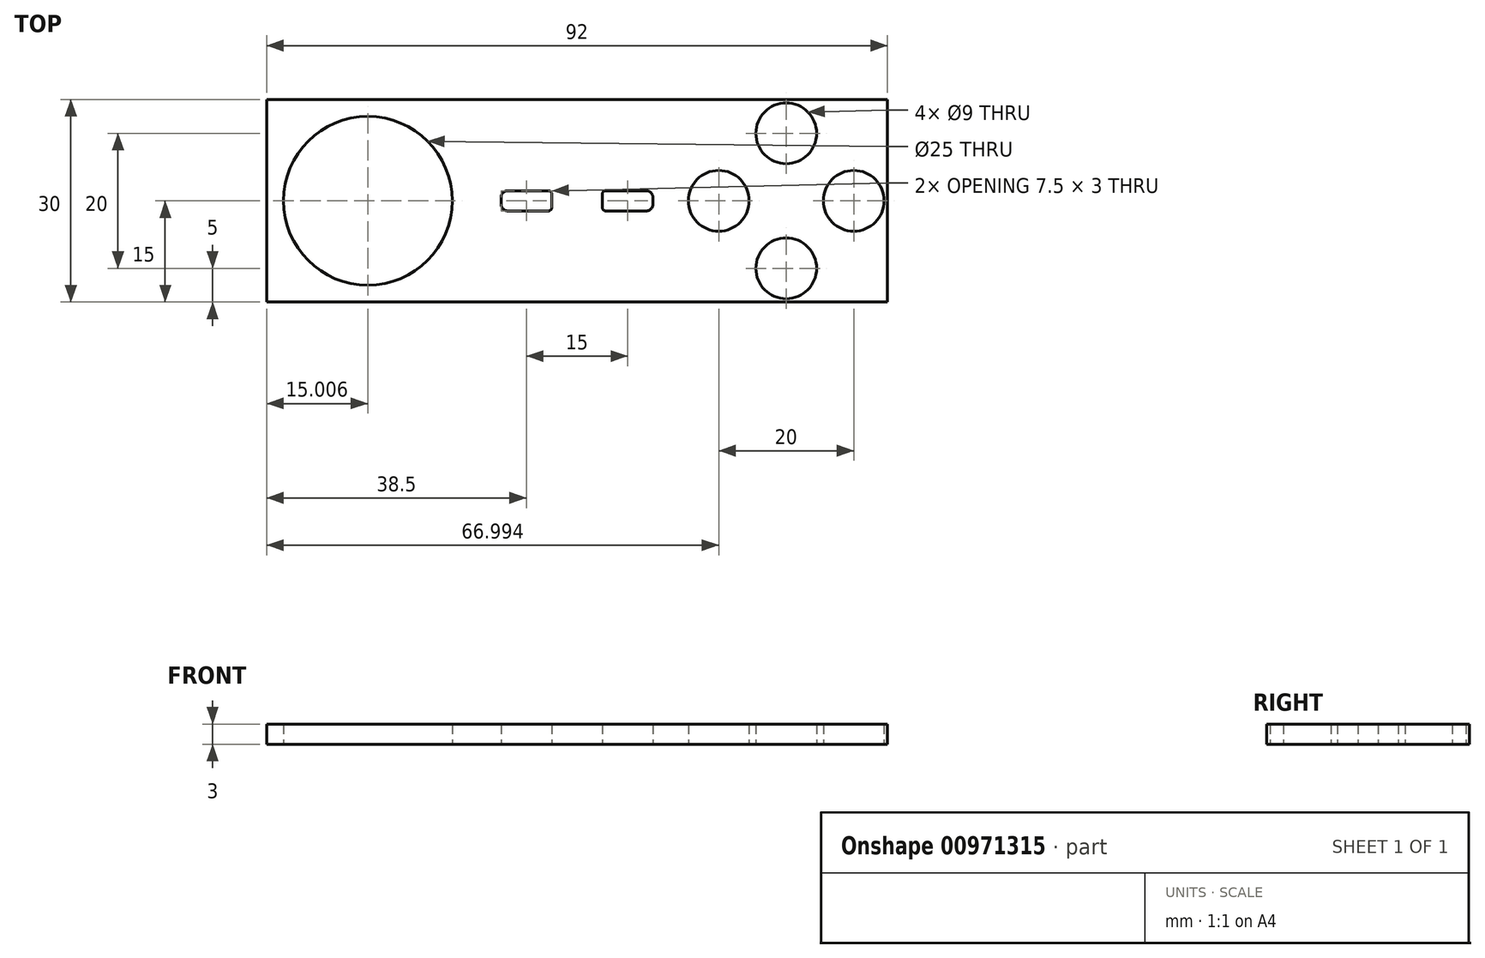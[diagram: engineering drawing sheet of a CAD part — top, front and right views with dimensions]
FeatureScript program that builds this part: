
annotation { "Feature Type Name" : "Feature", "Feature Type Description" : "" }
export const myFeature = defineFeature(function(context is Context, id is Id, definition is map)
    precondition{}
    {
        {
            var Q0;
            Q0=qCreatedBy(makeId("Top.planeOp"),FACE);
            var sketch = newSketch(context, id + "F0", { "sketchPlane" : qUnion([Q0])});
            skLineSegment(sketch, "E0.bottom", {"start": v(46, -15) * mm, "end": v(-46, -15) * mm});
            skLineSegment(sketch, "E0.top", {"start": v(46, 15) * mm, "end": v(-46, 15) * mm});
            skLineSegment(sketch, "E0.left", {"start": v(46, -15) * mm, "end": v(46, 15) * mm});
            skLineSegment(sketch, "E0.right", {"start": v(-46, -15) * mm, "end": v(-46, 15) * mm});
            skPoint(sketch, "E0.middle", {"position": v(0, 0) * mm});
            skCircle(sketch, "E1", {"center": v(-31, 0) * mm, "radius": 12.5 * mm});
            skPoint(sketch, "E2.start.orphan", {"position": v(-46, 0) * mm});
            skCircle(sketch, "E3", {"center": v(31, 10) * mm, "radius": 4.5 * mm});
            skCircle(sketch, "E4", {"center": v(21, 0) * mm, "radius": 4.5 * mm});
            skCircle(sketch, "E5", {"center": v(41, 0) * mm, "radius": 4.5 * mm});
            skCircle(sketch, "E6", {"center": v(31, -10) * mm, "radius": 4.5 * mm});
            skLineSegment(sketch, "E7.bottom", {"start": v(-4.25, -1.5) * mm, "end": v(-10.25, -1.5) * mm});
            skLineSegment(sketch, "E7.top", {"start": v(-4.25, 1.5) * mm, "end": v(-10.25, 1.5) * mm});
            skLineSegment(sketch, "E7.left", {"start": v(-3.75, -1) * mm, "end": v(-3.75, 1) * mm});
            skLineSegment(sketch, "E7.right", {"start": v(-11.25, -0.5) * mm, "end": v(-11.25, 0.5) * mm});
            skPoint(sketch, "E7.middle", {"position": v(-7.5, 0) * mm});
            skPoint(sketch, "E7.cornerSnap0", {"position": v(-3.75, 0) * mm});
            skLineSegment(sketch, "E8.bottom", {"start": v(4.25, -1.5) * mm, "end": v(10.25, -1.5) * mm});
            skLineSegment(sketch, "E8.top", {"start": v(4.25, 1.5) * mm, "end": v(10.25, 1.5) * mm});
            skLineSegment(sketch, "E8.left", {"start": v(3.75, -1) * mm, "end": v(3.75, 1) * mm});
            skLineSegment(sketch, "E8.right", {"start": v(11.25, -0.5) * mm, "end": v(11.25, 0.5) * mm});
            skPoint(sketch, "E8.middle", {"position": v(7.5, 0) * mm});
            skPoint(sketch, "E8.cornerSnap0", {"position": v(3.75, 0) * mm});
            skPoint(sketch, "E9.visualSharp", {"position": v(-11.25, 1.5) * mm});
            skArc(sketch, "E9.filletArc", {"start": v(-10.25, 1.5) * mm, "mid": v(-10.96, 1.2) * mm, "end": v(-11.25, 0.5) * mm});
            skPoint(sketch, "E10.visualSharp", {"position": v(-11.25, -1.5) * mm});
            skArc(sketch, "E10.filletArc", {"start": v(-11.25, -0.5) * mm, "mid": v(-10.96, -1.2) * mm, "end": v(-10.25, -1.5) * mm});
            skPoint(sketch, "E11.visualSharp", {"position": v(11.25, 1.5) * mm});
            skArc(sketch, "E11.filletArc", {"start": v(11.25, 0.5) * mm, "mid": v(10.96, 1.2) * mm, "end": v(10.25, 1.5) * mm});
            skPoint(sketch, "E12.visualSharp", {"position": v(11.25, -1.5) * mm});
            skArc(sketch, "E12.filletArc", {"start": v(10.25, -1.5) * mm, "mid": v(10.96, -1.2) * mm, "end": v(11.25, -0.5) * mm});
            skPoint(sketch, "E13.visualSharp", {"position": v(-3.75, -1.5) * mm});
            skArc(sketch, "E13.filletArc", {"start": v(-4.25, -1.5) * mm, "mid": v(-3.9, -1.35) * mm, "end": v(-3.75, -1) * mm});
            skPoint(sketch, "E14.visualSharp", {"position": v(-3.75, 1.5) * mm});
            skArc(sketch, "E14.filletArc", {"start": v(-3.75, 1) * mm, "mid": v(-3.9, 1.35) * mm, "end": v(-4.25, 1.5) * mm});
            skPoint(sketch, "E15.visualSharp", {"position": v(3.75, 1.5) * mm});
            skArc(sketch, "E15.filletArc", {"start": v(4.25, 1.5) * mm, "mid": v(3.9, 1.35) * mm, "end": v(3.75, 1) * mm});
            skPoint(sketch, "E16.visualSharp", {"position": v(3.75, -1.5) * mm});
            skArc(sketch, "E16.filletArc", {"start": v(3.75, -1) * mm, "mid": v(3.9, -1.35) * mm, "end": v(4.25, -1.5) * mm});
            skSolve(sketch);
        }
        {
            var Q0;
            Q0 = qSketchRegion(id + "F0", true);
            extrude(context, id + "F1", {"entities" : qUnion([Q0]), "depth" : 3 * mm, "offsetDistance" : 25 * mm});
        }
    });
